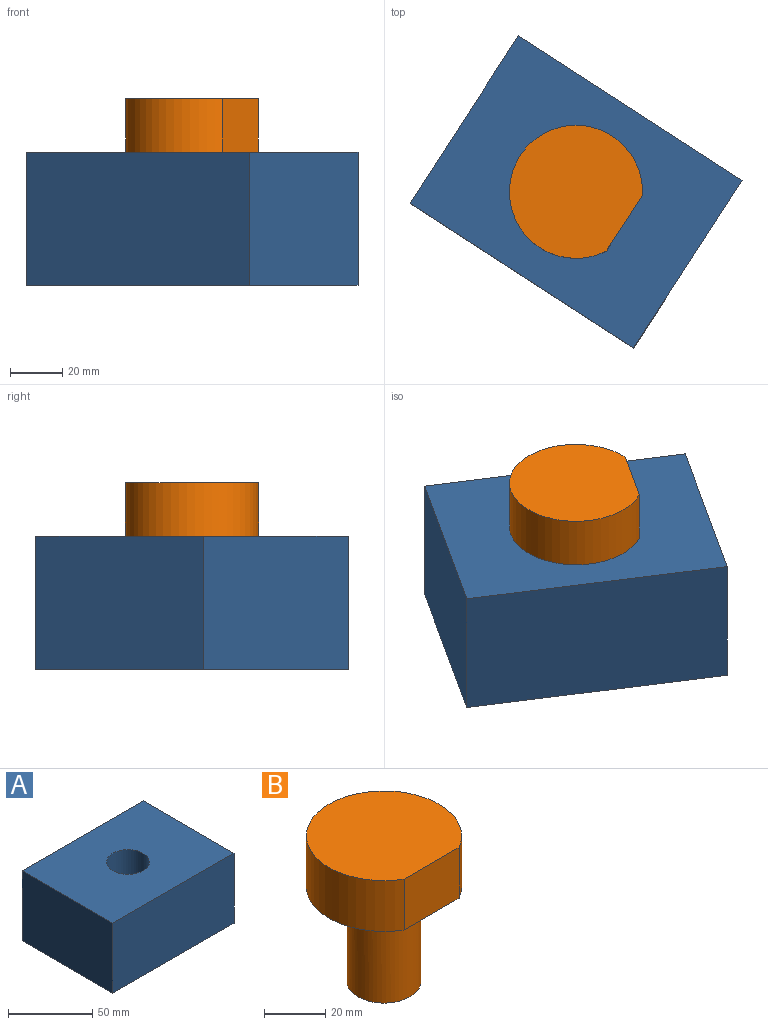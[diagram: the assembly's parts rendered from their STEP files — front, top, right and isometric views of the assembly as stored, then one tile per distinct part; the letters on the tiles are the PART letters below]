
ASSEMBLY  parts=2 mates=1
PART A: 7 faces, bbox 101.6x76.2x50.8 mm
  f0: plane 76.2x50.8mm, normal (1,0,0), area 3871mm2, adj f1,f3,f4,f5
  f1: plane 101.6x50.8mm, normal (0,1,0), area 5161.3mm2, adj f0,f2,f4,f5
  f2: plane 76.2x50.8mm, normal (-1,0,0), area 3871mm2, adj f1,f3,f4,f5
  f3: plane 101.6x50.8mm, normal (0,-1,0), area 5161.3mm2, adj f0,f2,f4,f5
  f4: plane 101.6x76.2mm, normal (0,0,1), area 7235.2mm2, adj f0,f1,f2,f3,f6
  f5: plane 101.6x76.2mm, normal (0,0,-1), area 7235.2mm2, adj f0,f1,f2,f3,f6
  f6: cylinder r=12.7mm len=50.8mm, axis (0,0,1), area 4053.7mm2, adj f4,f5
PART B: 6 faces, bbox 50.8x47.4x58.4 mm
  f0: cylinder r=25.4mm len=50.8mm, axis (0,0,-1), area 2702.4mm2, adj f1,f2,f3
  f1: plane 25.4x20.32mm, normal (0,-1,0), area 516.1mm2, adj f0,f2,f3
  f2: plane 50.8x47.4mm, normal (0,0,1), area 1968.4mm2, adj f0,f1
  f3: plane 50.8x47.4mm, normal (0,0,-1), area 1511.1mm2, adj f0,f1,f4
  f4: cylinder r=12.06mm len=38.1mm, axis (0,0,1), area 2888.2mm2, adj f3,f5
  f5: plane 24.13x24.13mm, normal (0,0,-1), area 457.3mm2, adj f4
PLACE A rot(axis=(0,0,-1),32.9deg) t=(65.3,-33.8,49.22)mm fixed
PLACE B rot(axis=(0,0,1),57.1deg) t=(65.3,-33.8,100.02)mm
MATE revolute A.f6 <-> B.f0  axis (0,0,1) through (65.3,-33.8,100.02)mm
